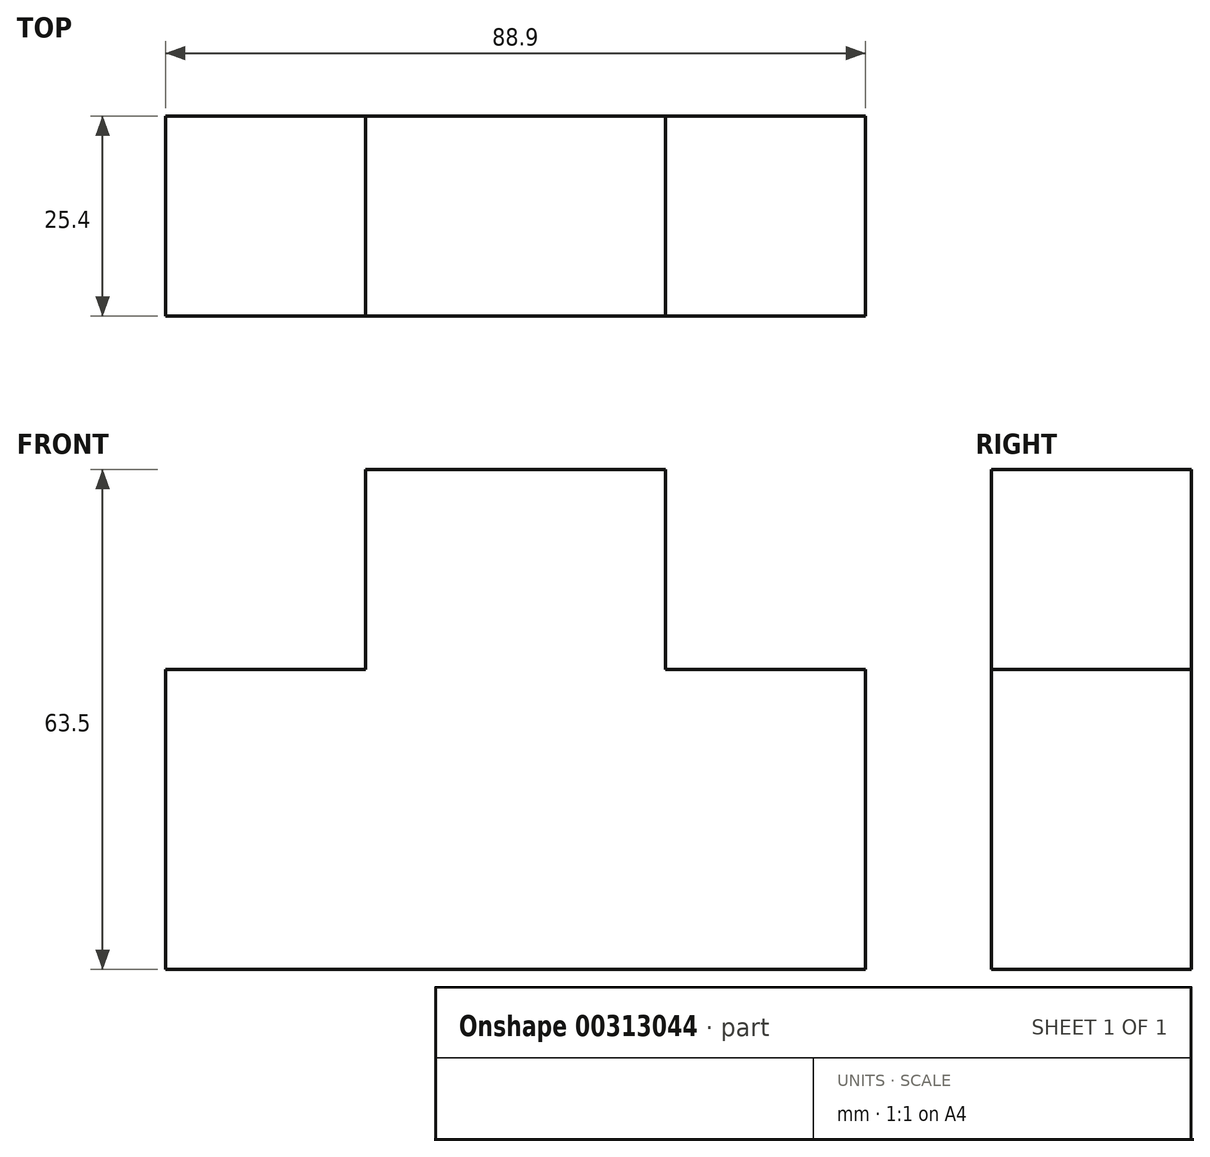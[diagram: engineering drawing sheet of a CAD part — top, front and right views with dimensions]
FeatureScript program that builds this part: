
annotation { "Feature Type Name" : "Feature", "Feature Type Description" : "" }
export const myFeature = defineFeature(function(context is Context, id is Id, definition is map)
    precondition{}
    {
        {
            var Q0;
            Q0=qCreatedBy(makeId("Front.planeOp"),FACE);
            var sketch = newSketch(context, id + "F0", { "sketchPlane" : qUnion([Q0])});
            skLineSegment(sketch, "E0", {"start": v(-123.59, -38.1) * mm, "end": v(-34.69, -38.1) * mm});
            skLineSegment(sketch, "E1", {"start": v(-34.69, -38.1) * mm, "end": v(-34.69, 0) * mm});
            skLineSegment(sketch, "E2", {"start": v(-34.69, 0) * mm, "end": v(-60.09, 0) * mm});
            skLineSegment(sketch, "E3", {"start": v(-60.09, 0) * mm, "end": v(-60.09, 25.4) * mm});
            skLineSegment(sketch, "E4", {"start": v(-60.09, 25.4) * mm, "end": v(-98.19, 25.4) * mm});
            skLineSegment(sketch, "E5", {"start": v(-98.19, 25.4) * mm, "end": v(-98.19, 0) * mm});
            skLineSegment(sketch, "E6", {"start": v(-98.19, 0) * mm, "end": v(-123.59, 0) * mm});
            skLineSegment(sketch, "E7", {"start": v(-123.59, 0) * mm, "end": v(-123.59, -38.1) * mm});
            skSolve(sketch);
        }
        {
            var Q0;
            Q0 = qSketchRegion(id + "F0", true);
            extrude(context, id + "F1", {"entities" : qUnion([Q0]), "depth" : 25.4 * mm});
        }
    });
